# Revit family: Sanitary_Other_Encon-Safety_Vertical-Showers-30-gpm-ABS-Hi-Viz-Shower-Head
name_source: partatom
category: Plumbing Fixtures
units: mm (PartAtom-declared; Revit-internal decimal feet)

## family parameters
Always vertical = Yes
Cut with Voids When Loaded = No
OmniClass Number = 23.45.05.14.24
OmniClass Title = Eye Wash Fountains
Part Type = Normal
Room Calculation Point = No
Round Connector Dimension = Use Diameter
Shared = No
Work Plane-Based = No

## types (1)
- 01052502
    Assembly Code = D2010600
    CW Connection = Yes
    CWFU = 0
    Depth = 0"
    Description = Vertical showers 30 gpm ABS Hi-Viz shower head
    Edition number = 1
    Flow = 30 GPM
    HW Connection = No
    HWFU = 0
    Heads Material = Encon Safety Products - Plastic - Acetal - Yellow
    Height = 43 1/2"
    Keynote = 15410
    Manufacturer = Encon Safety Products
    Model = 01052502
    Piping Material = Encon Safety Products - Metal - Steel Galvanized
    Product Guid = 7155e654-505d-43d8-a268-c4885b60186b
    Product data url = https://www.bimobject.com
    Supply Diameter = 1"
    URL = https://enconsafety.com
    Vent Connection = No
    WFU = 0
    Waste Connection = Yes
    Width = 15"

## geometry (parser evidence)
native form markers: Sweep x2
no freeform markers — native parametric forms only
